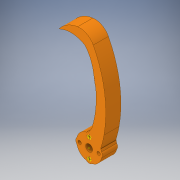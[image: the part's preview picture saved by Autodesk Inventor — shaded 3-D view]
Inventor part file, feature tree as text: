
AUTODESK INVENTOR PART (.ipt)
format: ipt  version: 2017 (Build 210142000, 142)  size: 444,416 bytes
history: native  units: in
note: dims shown in document units (in); Inventor stores cm internally (conversion verified against a paired STEP export)
features: sketch x27, extrude x26, fillet x11, chamfer x1
ambient origin geometry x8: Origin, YZ Plane, XZ Plane, XY Plane, X Axis, Y Axis, Z Axis, Center Point
bodies: Solid1 (feature_tree)
feature tree (65):
  extrude  "Extrusion1"  Depth=0.5in TaperAngle=0.0deg
  extrude  "Extrusion2"  Depth=0.5in TaperAngle=0.0deg
  extrude  "Extrusion3"  Depth=0.25in
  extrude  "Extrusion4"  Depth=0.5in
  extrude  "Extrusion5"  Depth=0.15in
  fillet  "Fillet1"  Radius=0.25in
  extrude  "Extrusion6"  Depth=0.25in
  extrude  "Extrusion7"  Depth=0.5in
  extrude  "Extrusion8"  Depth=0.5in TaperAngle=0.0deg
  extrude  "Extrusion9"  Depth=0.75in
  extrude  "Extrusion10"  Depth=0.5in
  fillet  "Fillet2"  [1 undecoded]
  fillet  "Fillet3"  Radius=1.0in
  fillet  "Fillet4"  Radius=0.5in
  fillet  "Fillet5"  Radius=0.5in
  fillet  "Fillet6"  Radius=0.5in
  extrude  "Extrusion11"  Depth=0.5in
  extrude  "Extrusion12"  Depth=0.5in
  fillet  "Fillet7"  Radius=0.5in
  extrude  "Extrusion13"  Depth=0.5in TaperAngle=0.0deg
  fillet  "Fillet8"  Radius=0.5in
  fillet  "Fillet9"  Radius=0.5in
  extrude  "Extrusion14"  Depth=0.5in
  extrude  "Extrusion15"  Depth=0.5in TaperAngle=0.0deg
  chamfer  "Chamfer1"  Distance=0.5in
  fillet  "Fillet10"  Radius=0.125in
  extrude  "Extrusion16"  Depth=0.5in TaperAngle=0.0deg
  extrude  "Extrusion17"  Depth=0.5in TaperAngle=0.0deg
  extrude  "Extrusion18"  Depth=0.055in
  extrude  "Extrusion19"  Depth=0.125in
  extrude  "Extrusion20"  Depth=0.11in
  extrude  "Extrusion21"  Depth=0.125in
  extrude  "Extrusion22"  Depth=0.5in TaperAngle=0.0deg
  extrude  "Extrusion23"  TaperAngle=90.0deg  [1 undecoded]
  extrude  "Extrusion24"  Depth=0.5in TaperAngle=0.0deg
  extrude  "Extrusion25"  Depth=0.5in
  sketch  "Sketch26"  dims[d83=0.5in d84=0.0in d85=0.3125in d86=0.11in]
  fillet  "Fillet11"  Radius=0.11in
  extrude  "Extrusion26"  Depth=0.5in
  sketch  "Sketch1"  dims[d0=1.0in d1=0.5in d2=0.0in]
  sketch  "Sketch2"  dims[d3=0.3in d4=0.5in d5=0.0in]
  sketch  "Sketch3"  dims[d6=0.145in d7=0.25in]
  sketch  "Sketch4"  dims[d8=0.5in d9=0.0in d10=0.15in]
  sketch  "Sketch5"  dims[d11=0.15in d12=0.15in d13=0.25in]
  sketch  "Sketch6"  dims[d14=0.25in d15=0.25in]
  sketch  "Sketch7"  dims[d16=0.5in d17=0.0in d18=1.5in]
  sketch  "Sketch8"  dims[d19=90.0deg d20=0.5in d21=0.0in]
  sketch  "Sketch9"  dims[d22=0.25in d23=0.75in]
  sketch  "Sketch10"  dims[d24=1.0in d25=0.0in d26=2.3in d27=90.0deg d28=1.0in d29=0.5in d30=0.0in d31=0.5in d32=0.0in d33=0.5in d34=0.0in]
  sketch  "Sketch11"  dims[d35=0.5in d36=0.0in d37=0.25in]
  sketch  "Sketch12"  dims[d38=0.5in d39=0.5in d40=0.5in]
  sketch  "Sketch13"  dims[d41=0.125in d42=0.5in d43=0.0in d44=0.5in d45=0.0in d46=0.5in]
  sketch  "Sketch14"  dims[d47=0.5in d48=0.0in d49=5.0in]
  sketch  "Sketch15"  dims[d50=0.125in d51=0.5in d52=0.0in d53=0.5in d54=0.0in]
  sketch  "Sketch16"  dims[d55=0.25in d56=0.125in d57=45.0deg d58=0.125in]
  sketch  "Sketch17"  dims[d59=0.5in d60=0.0in d61=0.5in d62=0.0in]
  sketch  "Sketch18"  dims[d63=0.23in d64=0.5in d65=0.0in]
  sketch  "Sketch19"  dims[d66=0.07in d67=0.055in]
  sketch  "Sketch20"  dims[d68=0.11in d69=0.125in]
  sketch  "Sketch21"  dims[d70=0.11in d71=0.11in]
  sketch  "Sketch22"  dims[d72=0.11in d73=0.125in]
  sketch  "Sketch23"  dims[d74=0.125in d75=0.5in d76=0.0in]
  sketch  "Sketch24"  dims[d77=2.3in d78=90.0deg]
  sketch  "Sketch25"  dims[d79=0.5in d80=0.0in d81=0.5in d82=0.0in]
  sketch  "Sketch27"  dims[d87=0.3125in d88=0.11in d89=0.313in d90=0.11in d91=0.313in d92=0.11in d93=0.5in d94=0.0in d95=0.5in d96=0.0in d97=0.11in d98=0.5in d99=0.0in d100=0.5in d101=0.5in d102=0.0in]
note: 2 required parameter values undecoded (feature->parameter linkage not recoverable at this tier; creation-order binding heuristic only, values carry confidence <= 0.55)
